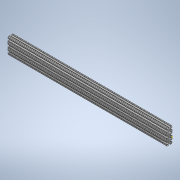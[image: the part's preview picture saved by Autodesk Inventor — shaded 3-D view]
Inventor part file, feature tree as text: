
AUTODESK INVENTOR PART (.ipt)
format: ipt  version: 2020 (Build 240168000, 168)  size: 387,072 bytes
history: native  units: in
note: dims shown in document units (in); Inventor stores cm internally (conversion verified against a paired STEP export)
features: sketch x2, extrude x1
ambient origin geometry x8: Origin, YZ Plane, XZ Plane, XY Plane, X Axis, Y Axis, Z Axis, Center Point
bodies: Solid1 (feature_tree)
feature tree (3):
  extrude  "Extrusion1"  [1 undecoded]
  sketch  "Sketch2"
  sketch  "Sketch1"  dims[d0=30.0in d1=0.0in]
note: 1 required parameter value undecoded (feature->parameter linkage not recoverable at this tier; creation-order binding heuristic only, values carry confidence <= 0.55)
